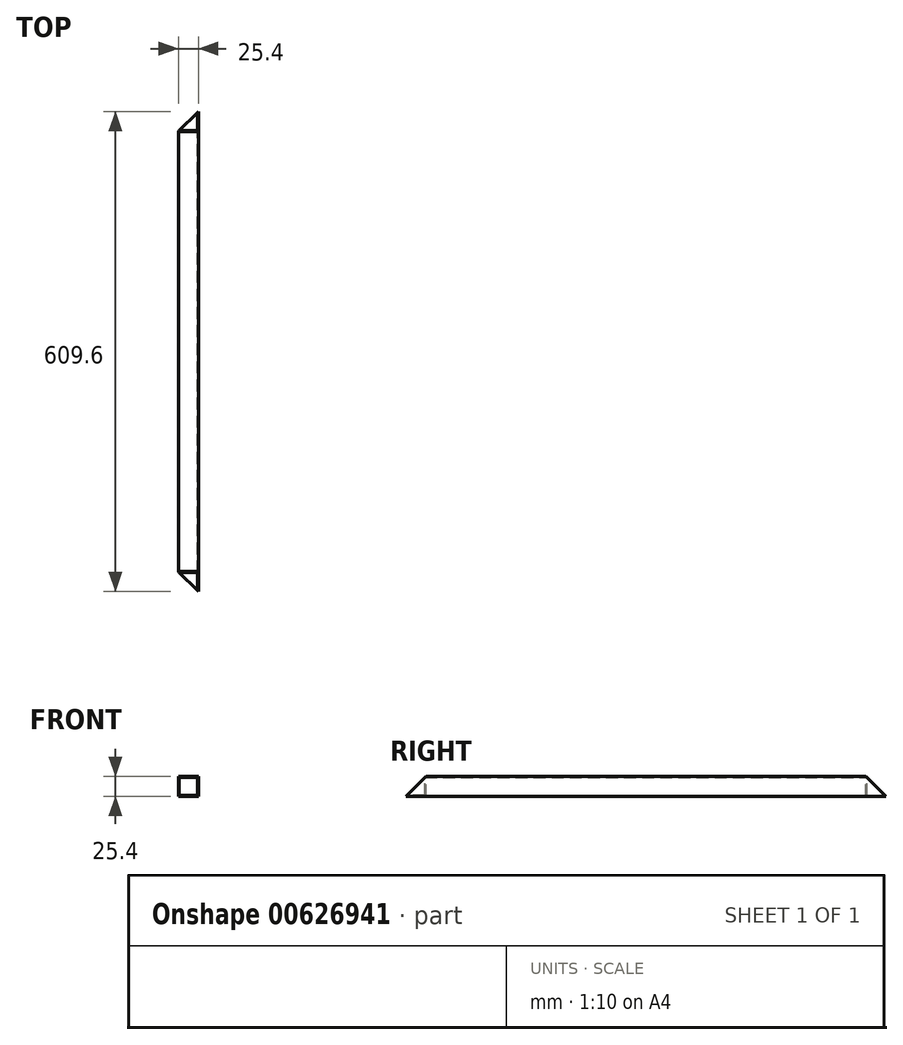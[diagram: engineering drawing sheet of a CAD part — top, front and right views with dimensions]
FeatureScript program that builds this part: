
annotation { "Feature Type Name" : "Feature", "Feature Type Description" : "" }
export const myFeature = defineFeature(function(context is Context, id is Id, definition is map)
    precondition{}
    {
        {
            var Q0;
            Q0=qCreatedBy(makeId("Front.planeOp"),FACE);
            var sketch = newSketch(context, id + "F0", { "sketchPlane" : qUnion([Q0])});
            skLineSegment(sketch, "E0.bottom", {"start": v(12.7, 12.7) * mm, "end": v(-12.7, 12.7) * mm});
            skLineSegment(sketch, "E0.top", {"start": v(12.7, -12.7) * mm, "end": v(-12.7, -12.7) * mm});
            skLineSegment(sketch, "E0.left", {"start": v(12.7, 12.7) * mm, "end": v(12.7, -12.7) * mm});
            skLineSegment(sketch, "E0.right", {"start": v(-12.7, 12.7) * mm, "end": v(-12.7, -12.7) * mm});
            skPoint(sketch, "E0.middle", {"position": v(0, 0) * mm});
            skLineSegment(sketch, "E1.bottom", {"start": v(11.46, 11.46) * mm, "end": v(-11.46, 11.46) * mm});
            skLineSegment(sketch, "E1.top", {"start": v(11.46, -11.46) * mm, "end": v(-11.46, -11.46) * mm});
            skLineSegment(sketch, "E1.left", {"start": v(11.46, 11.46) * mm, "end": v(11.46, -11.46) * mm});
            skLineSegment(sketch, "E1.right", {"start": v(-11.46, 11.46) * mm, "end": v(-11.46, -11.46) * mm});
            skSolve(sketch);
        }
        {
            var Q0;
            Q0=makeQuery(id+"F0.imprint","IMPRINT",FACE,{"disambiguationData":[TD([[makeQuery(id+"F0.imprint","IMPRINT",EDGE,{"derivedFrom":sQuery(id+"F0.wireOp",EDGE,"E0.bottom")}),1.0]])]});
            extrude(context, id + "F1", {"entities" : qUnion([Q0]), "depth" : 609.6 * mm, "offsetDistance" : 25 * mm});
        }
        {
            var Q0;
            Q0=makeQuery(id+"F1.opExtrude","SWEPT_FACE",FACE,{"disambiguationData":[OSD([sQuery(id+"F0.wireOp",EDGE,"E0.bottom")])]});
            var sketch = newSketch(context, id + "F2", { "sketchPlane" : qUnion([Q0])});
            skLineSegment(sketch, "E2", {"start": v(12.7, -609.6) * mm, "end": v(-12.7, -584.2) * mm});
            skLineSegment(sketch, "E3", {"start": v(-12.7, -584.2) * mm, "end": v(-12.7, -609.6) * mm});
            skLineSegment(sketch, "E4", {"start": v(-12.7, -609.6) * mm, "end": v(12.7, -609.6) * mm});
            skLineSegment(sketch, "E5", {"start": v(-12.7, -304.8) * mm, "end": v(-173.17, -304.8) * mm, "construction": true});
            skLineSegment(sketch, "E6.MirrorCS", {"start": v(12.7, 0) * mm, "end": v(-12.7, -25.4) * mm});
            skLineSegment(sketch, "E7.MirrorCS", {"start": v(-12.7, 0) * mm, "end": v(12.7, 0) * mm});
            skLineSegment(sketch, "E8.MirrorCS", {"start": v(-12.7, -25.4) * mm, "end": v(-12.7, 0) * mm});
            skSolve(sketch);
        }
        {
            var Q0;
            Q0=makeQuery(id+"F2.imprint","IMPRINT",FACE,{"disambiguationData":[TD([[makeQuery(id+"F2.imprint","IMPRINT",EDGE,{"derivedFrom":sQuery(id+"F2.wireOp",EDGE,"E6.MirrorCS")}),-1.0]])]});
            var Q1;
            Q1=makeQuery(id+"F2.imprint","IMPRINT",FACE,{"disambiguationData":[TD([[makeQuery(id+"F2.imprint","IMPRINT",EDGE,{"derivedFrom":sQuery(id+"F2.wireOp",EDGE,"E2")}),1.0]])]});
            extrude(context, id + "F3", {"entities" : qUnion([Q0, Q1]), "operationType" : NewBodyOperationType.REMOVE, "endBound" : BoundingType.THROUGH_ALL, "oppositeDirection" : true, "depth" : 25 * mm, "offsetDistance" : 25 * mm});
        }
        {
            var Q0;
            Q0=makeQuery(id+"F1.opExtrude","SWEPT_FACE",FACE,{"disambiguationData":[OSD([sQuery(id+"F0.wireOp",EDGE,"E0.left")])]});
            var sketch = newSketch(context, id + "F4", { "sketchPlane" : qUnion([Q0])});
            skLineSegment(sketch, "E9", {"start": v(-609.6, -12.7) * mm, "end": v(-584.2, 12.7) * mm});
            skLineSegment(sketch, "E10", {"start": v(-584.2, 12.7) * mm, "end": v(-609.6, 12.7) * mm});
            skLineSegment(sketch, "E11", {"start": v(-609.6, 12.7) * mm, "end": v(-609.6, -12.7) * mm});
            skLineSegment(sketch, "E12", {"start": v(-304.8, 12.7) * mm, "end": v(-304.8, 78.96) * mm, "construction": true});
            skLineSegment(sketch, "E13.MirrorCS", {"start": v(0, -12.7) * mm, "end": v(-25.4, 12.7) * mm});
            skLineSegment(sketch, "E14.MirrorCS", {"start": v(-25.4, 12.7) * mm, "end": v(0, 12.7) * mm});
            skLineSegment(sketch, "E15.MirrorCS", {"start": v(0, 12.7) * mm, "end": v(0, -12.7) * mm});
            skSolve(sketch);
        }
        {
            var Q0;
            Q0=makeQuery(id+"F4.imprint","IMPRINT",FACE,{"disambiguationData":[TD([[makeQuery(id+"F4.imprint","IMPRINT",EDGE,{"derivedFrom":sQuery(id+"F4.wireOp",EDGE,"E9")}),1.0]])]});
            var Q1;
            Q1=makeQuery(id+"F4.imprint","IMPRINT",FACE,{"disambiguationData":[TD([[makeQuery(id+"F4.imprint","IMPRINT",EDGE,{"derivedFrom":sQuery(id+"F4.wireOp",EDGE,"E13.MirrorCS")}),-1.0]])]});
            extrude(context, id + "F5", {"entities" : qUnion([Q0, Q1]), "operationType" : NewBodyOperationType.REMOVE, "endBound" : BoundingType.THROUGH_ALL, "oppositeDirection" : true, "depth" : 25 * mm, "offsetDistance" : 25 * mm});
        }
    });
